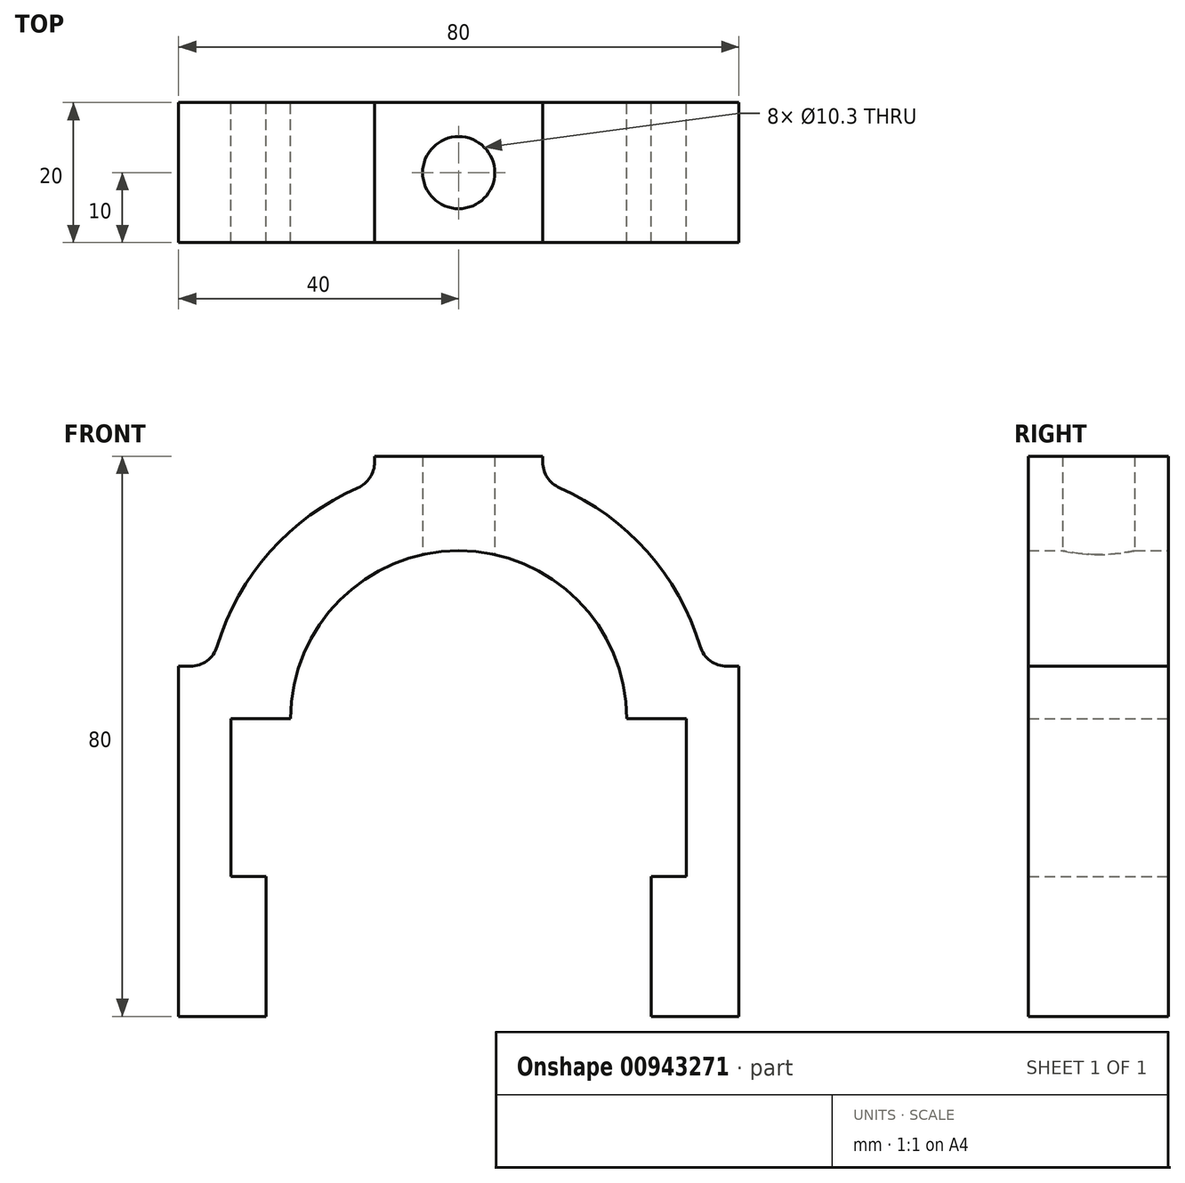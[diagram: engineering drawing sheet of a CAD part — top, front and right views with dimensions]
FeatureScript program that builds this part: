
annotation { "Feature Type Name" : "Feature", "Feature Type Description" : "" }
export const myFeature = defineFeature(function(context is Context, id is Id, definition is map)
    precondition{}
    {
        {
            var Q0;
            Q0=qCreatedBy(makeId("Front.planeOp"),FACE);
            var sketch = newSketch(context, id + "F0", { "sketchPlane" : qUnion([Q0])});
            skLineSegment(sketch, "E0", {"start": v(0, 51.15) * mm, "end": v(0, -47.63) * mm, "construction": true});
            skArc(sketch, "E1", {"start": v(-14.4, 33) * mm, "mid": v(-26.94, 23.88) * mm, "end": v(-34.48, 10.35) * mm});
            skArc(sketch, "E2", {"start": v(0, 24) * mm, "mid": v(-16.97, 16.97) * mm, "end": v(-24, 0) * mm});
            skLineSegment(sketch, "E3", {"start": v(-40, -42.5) * mm, "end": v(-27.5, -42.5) * mm});
            skLineSegment(sketch, "E4", {"start": v(-27.5, -42.5) * mm, "end": v(-27.5, -22.5) * mm});
            skLineSegment(sketch, "E5", {"start": v(-27.5, -22.5) * mm, "end": v(-32.5, -22.5) * mm});
            skLineSegment(sketch, "E6", {"start": v(-40, -42.5) * mm, "end": v(-40, 7.5) * mm});
            skLineSegment(sketch, "E7", {"start": v(-40, 7.5) * mm, "end": v(-38.31, 7.5) * mm});
            skLineSegment(sketch, "E8", {"start": v(-24, 0) * mm, "end": v(-32.5, 0) * mm});
            skLineSegment(sketch, "E9", {"start": v(-32.5, 0) * mm, "end": v(-32.5, -22.5) * mm});
            skLineSegment(sketch, "E10", {"start": v(-12, 36.66) * mm, "end": v(-12, 37.5) * mm});
            skLineSegment(sketch, "E11", {"start": v(-12, 37.5) * mm, "end": v(0, 37.5) * mm});
            skLineSegment(sketch, "E12.MirrorCS", {"start": v(40, -42.5) * mm, "end": v(27.5, -42.5) * mm});
            skLineSegment(sketch, "E13.MirrorCS", {"start": v(27.5, -42.5) * mm, "end": v(27.5, -22.5) * mm});
            skLineSegment(sketch, "E14.MirrorCS", {"start": v(27.5, -22.5) * mm, "end": v(32.5, -22.5) * mm});
            skLineSegment(sketch, "E15.MirrorCS", {"start": v(32.5, 0) * mm, "end": v(32.5, -22.5) * mm});
            skLineSegment(sketch, "E16.MirrorCS", {"start": v(24, 0) * mm, "end": v(32.5, 0) * mm});
            skArc(sketch, "E17.MirrorCS", {"start": v(0, 24) * mm, "mid": v(16.97, 16.97) * mm, "end": v(24, 0) * mm});
            skLineSegment(sketch, "E18.MirrorCS", {"start": v(12, 37.5) * mm, "end": v(0, 37.5) * mm});
            skLineSegment(sketch, "E19.MirrorCS", {"start": v(12, 36.66) * mm, "end": v(12, 37.5) * mm});
            skArc(sketch, "E20.MirrorCS", {"start": v(14.4, 33) * mm, "mid": v(26.94, 23.88) * mm, "end": v(34.48, 10.35) * mm});
            skLineSegment(sketch, "E21.MirrorCS", {"start": v(40, 7.5) * mm, "end": v(38.31, 7.5) * mm});
            skLineSegment(sketch, "E22.MirrorCS", {"start": v(40, -42.5) * mm, "end": v(40, 7.5) * mm});
            skPoint(sketch, "E23.visualSharp", {"position": v(35.21, 7.5) * mm});
            skArc(sketch, "E23.filletArc", {"start": v(34.48, 10.35) * mm, "mid": v(35.92, 8.3) * mm, "end": v(38.31, 7.5) * mm});
            skPoint(sketch, "E24.visualSharp", {"position": v(12, 33.94) * mm});
            skArc(sketch, "E24.filletArc", {"start": v(12, 36.66) * mm, "mid": v(12.65, 34.47) * mm, "end": v(14.4, 33) * mm});
            skPoint(sketch, "E25.visualSharp", {"position": v(-12, 33.94) * mm});
            skArc(sketch, "E25.filletArc", {"start": v(-14.4, 33) * mm, "mid": v(-12.65, 34.47) * mm, "end": v(-12, 36.66) * mm});
            skPoint(sketch, "E26.visualSharp", {"position": v(-35.21, 7.5) * mm});
            skArc(sketch, "E26.filletArc", {"start": v(-38.31, 7.5) * mm, "mid": v(-35.92, 8.3) * mm, "end": v(-34.48, 10.35) * mm});
            skSolve(sketch);
        }
        {
            var Q0;
            Q0=qSketchRegion(id+"F0",true);
            extrude(context, id + "F1", {"entities" : qUnion([Q0]), "depth" : 20 * mm, "offsetDistance" : 25 * mm, "symmetric" : true});
        }
        {
            var Q0;
            Q0=qCreatedBy(makeId("Top.planeOp"),FACE);
            var sketch = newSketch(context, id + "F2", { "sketchPlane" : qUnion([Q0])});
            skCircle(sketch, "E27", {"center": v(0, 0) * mm, "radius": 5.15 * mm});
            skSolve(sketch);
        }
        {
            var Q0;
            Q0=sQuery(id+"F2.wireOp",VERTEX,"E27.center");
            var Q1;
            Q1=makeQuery(id+"F1.opExtrude","SWEPT_BODY",BODY,{"disambiguationData":[OSD([sQuery(id+"F0.wireOp",EDGE,"E1"),sQuery(id+"F0.wireOp",EDGE,"E2"),sQuery(id+"F0.wireOp",EDGE,"E3"),sQuery(id+"F0.wireOp",EDGE,"E4"),sQuery(id+"F0.wireOp",EDGE,"E5"),sQuery(id+"F0.wireOp",EDGE,"E6"),sQuery(id+"F0.wireOp",EDGE,"E7"),sQuery(id+"F0.wireOp",EDGE,"E9"),sQuery(id+"F0.wireOp",EDGE,"E8"),sQuery(id+"F0.wireOp",EDGE,"E10"),sQuery(id+"F0.wireOp",EDGE,"E11"),sQuery(id+"F0.wireOp",EDGE,"E12.MirrorCS"),sQuery(id+"F0.wireOp",EDGE,"E13.MirrorCS"),sQuery(id+"F0.wireOp",EDGE,"E14.MirrorCS"),sQuery(id+"F0.wireOp",EDGE,"E15.MirrorCS"),sQuery(id+"F0.wireOp",EDGE,"E16.MirrorCS"),sQuery(id+"F0.wireOp",EDGE,"E17.MirrorCS"),sQuery(id+"F0.wireOp",EDGE,"E18.MirrorCS"),sQuery(id+"F0.wireOp",EDGE,"E19.MirrorCS"),sQuery(id+"F0.wireOp",EDGE,"E20.MirrorCS"),sQuery(id+"F0.wireOp",EDGE,"E21.MirrorCS"),sQuery(id+"F0.wireOp",EDGE,"E22.MirrorCS"),sQuery(id+"F0.wireOp",EDGE,"E23.filletArc"),sQuery(id+"F0.wireOp",EDGE,"E24.filletArc"),sQuery(id+"F0.wireOp",EDGE,"E25.filletArc"),sQuery(id+"F0.wireOp",EDGE,"E26.filletArc")])]});
            hole(context, id + "F3", {"style" : HoleStyle.SIMPLE, "endStyle" : HoleEndStyle.THROUGH, "oppositeDirection" : true, "standardTappedOrClearance" : lookupTablePath({ "standard" : "ISO", "engagement" : "75%", "pitch" : "1.75 mm", "size" : "M12", "type" : "Tapped" }), "standardBlindInLast" : lookupTablePath({ "standard" : "ISO", "fit" : "Normal", "engagement" : "75%", "pitch" : "1.75 mm", "size" : "M12", "type" : "Clearance & tapped" }), "holeDiameter" : 10.3 * mm, "majorDiameter" : 12 * mm, "showTappedDepth" : true, "isTappedThrough" : true, "tappedDepth" : 12 * mm, "tapClearance" : 3, "locations" : qUnion([Q0]), "scope" : qUnion([Q1])});
        }
    });
